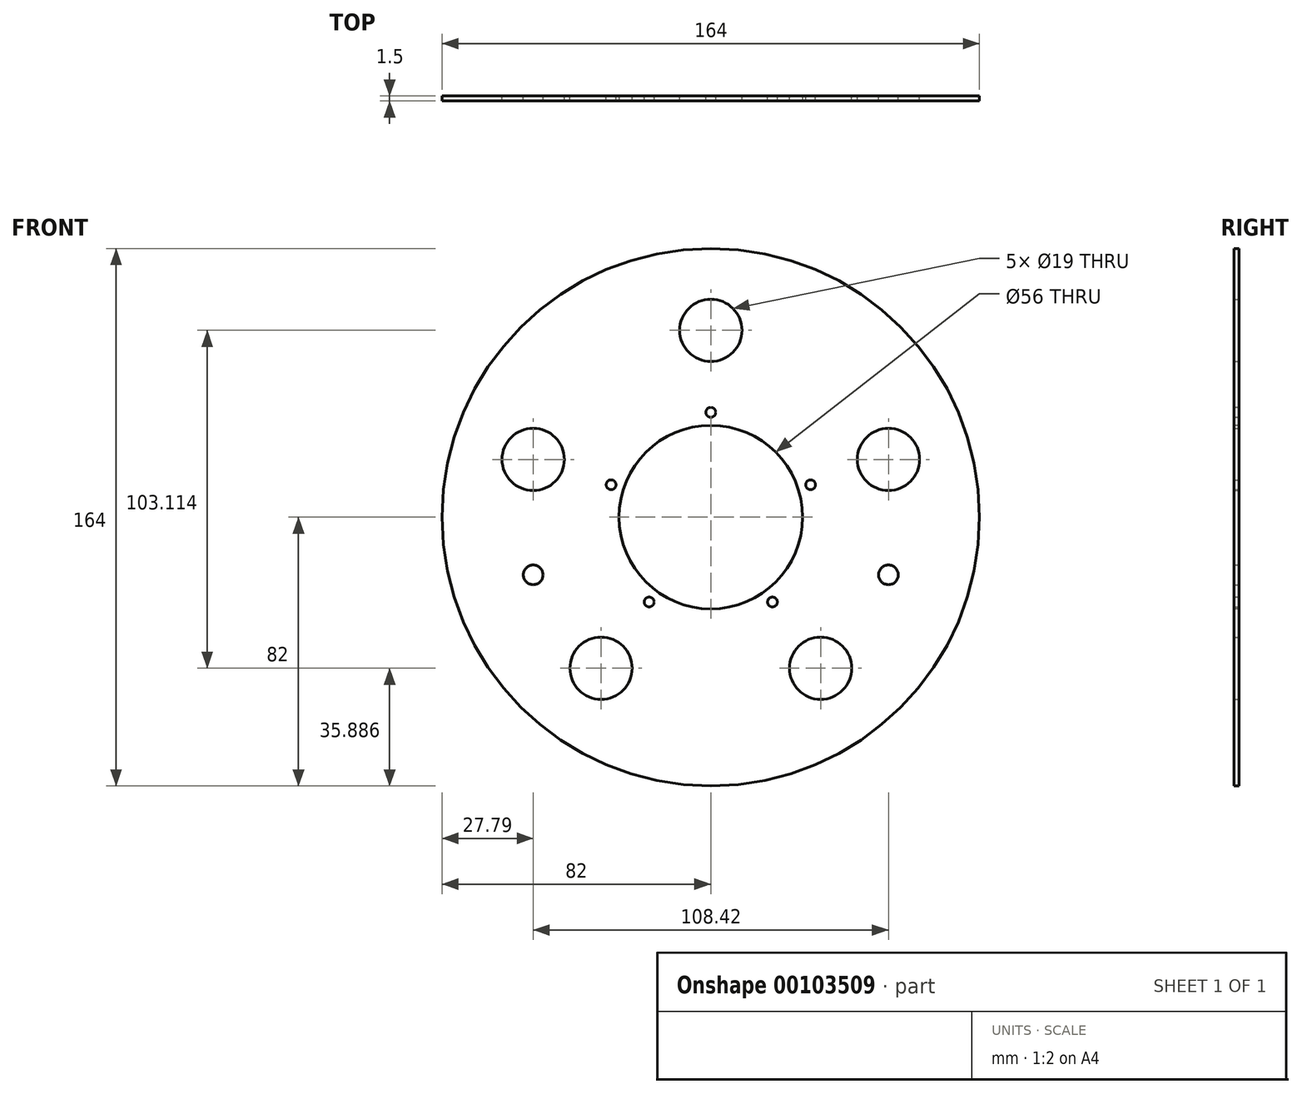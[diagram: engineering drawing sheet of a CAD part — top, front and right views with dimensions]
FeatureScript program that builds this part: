
annotation { "Feature Type Name" : "Feature", "Feature Type Description" : "" }
export const myFeature = defineFeature(function(context is Context, id is Id, definition is map)
    precondition{}
    {
        {
            var Q0;
            Q0=qCreatedBy(makeId("Front.planeOp"),FACE);
            var sketch = newSketch(context, id + "F0", { "sketchPlane" : qUnion([Q0])});
            skCircle(sketch, "E0", {"center": v(0, 0) * mm, "radius": 82 * mm});
            skCircle(sketch, "E1", {"center": v(0, 0) * mm, "radius": 57 * mm, "construction": true});
            skPoint(sketch, "E2", {"position": v(0, 57) * mm});
            skPoint(sketch, "E3", {"position": v(54.21, 17.61) * mm});
            skPoint(sketch, "E4", {"position": v(-54.21, 17.61) * mm});
            skPoint(sketch, "E5", {"position": v(-33.5, -46.11) * mm});
            skPoint(sketch, "E6", {"position": v(33.5, -46.11) * mm});
            skPoint(sketch, "E7", {"position": v(-54.21, -17.61) * mm});
            skPoint(sketch, "E8", {"position": v(54.21, -17.61) * mm});
            skLineSegment(sketch, "E9", {"start": v(0, 0) * mm, "end": v(-54.21, 17.61) * mm, "construction": true});
            skLineSegment(sketch, "E10", {"start": v(0, 0) * mm, "end": v(-54.21, -17.61) * mm, "construction": true});
            skCircle(sketch, "E11", {"center": v(0, 0) * mm, "radius": 32 * mm});
            skLineSegment(sketch, "E12", {"start": v(33.5, -46.11) * mm, "end": v(0, 0) * mm, "construction": true});
            skLineSegment(sketch, "E13", {"start": v(0, 0) * mm, "end": v(-33.5, -46.11) * mm, "construction": true});
            skLineSegment(sketch, "E14", {"start": v(0, 0) * mm, "end": v(0, 57) * mm, "construction": true});
            skLineSegment(sketch, "E15", {"start": v(0, 0) * mm, "end": v(54.21, 17.61) * mm, "construction": true});
            skPoint(sketch, "E16", {"position": v(18.8, -25.89) * mm});
            skPoint(sketch, "E17", {"position": v(30.43, 9.89) * mm});
            skPoint(sketch, "E18", {"position": v(-18.8, -25.89) * mm});
            skPoint(sketch, "E19", {"position": v(-30.43, 9.89) * mm});
            skPoint(sketch, "E20", {"position": v(0, 32) * mm});
            skCircle(sketch, "E21", {"center": v(0, 0) * mm, "radius": 28 * mm});
            skSolve(sketch);
        }
        {
            var Q0;
            Q0=makeQuery(id+"F0.imprint","IMPRINT",FACE,{"disambiguationData":[TD([[makeQuery(id+"F0.imprint","IMPRINT",EDGE,{"derivedFrom":sQuery(id+"F0.wireOp",EDGE,"E11")}),1.0]])]});
            var Q1;
            Q1=makeQuery(id+"F0.imprint","IMPRINT",FACE,{"disambiguationData":[TD([[makeQuery(id+"F0.imprint","IMPRINT",EDGE,{"derivedFrom":sQuery(id+"F0.wireOp",EDGE,"E0")}),1.0]])]});
            extrude(context, id + "F1", {"entities" : qUnion([Q0, Q1]), "oppositeDirection" : true, "depth" : 1.5 * mm});
        }
        {
            var Q0;
            Q0=sQuery(id+"F0.wireOp",VERTEX,"E2");
            var Q1;
            Q1=sQuery(id+"F0.wireOp",VERTEX,"E3");
            var Q2;
            Q2=sQuery(id+"F0.wireOp",VERTEX,"E6");
            var Q3;
            Q3=sQuery(id+"F0.wireOp",VERTEX,"E5");
            var Q4;
            Q4=sQuery(id+"F0.wireOp",VERTEX,"E4");
            var Q5;
            Q5=makeQuery(id+"F1.opExtrude","SWEPT_BODY",BODY,{"disambiguationData":[OSD([sQuery(id+"F0.wireOp",EDGE,"E0")])]});
            hole(context, id + "F2", {"style" : HoleStyle.SIMPLE, "endStyle" : HoleEndStyle.THROUGH, "standardTappedOrClearance" : lookupTablePath({ "standard" : "ISO", "size" : "19", "type" : "Drilled" }), "standardBlindInLast" : lookupTablePath({ "standard" : "ISO", "size" : "19", "type" : "Drilled" }), "holeDiameter" : 19 * mm, "locations" : qUnion([Q0, Q1, Q2, Q3, Q4]), "scope" : qUnion([Q5]), "isTappedThrough" : true, "startStyle" : HoleStartStyle.PART});
        }
        {
            var Q0;
            Q0=sQuery(id+"F0.wireOp",VERTEX,"E7");
            var Q1;
            Q1=sQuery(id+"F0.wireOp",VERTEX,"E8");
            var Q2;
            Q2=makeQuery(id+"F1.opExtrude","SWEPT_BODY",BODY,{"disambiguationData":[OSD([sQuery(id+"F0.wireOp",EDGE,"E0")])]});
            hole(context, id + "F3", {"style" : HoleStyle.SIMPLE, "endStyle" : HoleEndStyle.THROUGH, "standardTappedOrClearance" : lookupTablePath({ "standard" : "ISO", "size" : "6", "type" : "Drilled" }), "standardBlindInLast" : lookupTablePath({ "standard" : "ISO", "size" : "6", "type" : "Drilled" }), "holeDiameter" : 6 * mm, "locations" : qUnion([Q0, Q1]), "scope" : qUnion([Q2]), "isTappedThrough" : true, "startStyle" : HoleStartStyle.SKETCH});
        }
        {
            var Q0;
            Q0=sQuery(id+"F0.wireOp",VERTEX,"E16");
            var Q1;
            Q1=sQuery(id+"F0.wireOp",VERTEX,"E17");
            var Q2;
            Q2=sQuery(id+"F0.wireOp",VERTEX,"E18");
            var Q3;
            Q3=sQuery(id+"F0.wireOp",VERTEX,"E19");
            var Q4;
            Q4=sQuery(id+"F0.wireOp",VERTEX,"E20");
            var Q5;
            Q5=makeQuery(id+"F1.opExtrude","SWEPT_BODY",BODY,{"disambiguationData":[OSD([sQuery(id+"F0.wireOp",EDGE,"E0")])]});
            hole(context, id + "F4", {"style" : HoleStyle.SIMPLE, "endStyle" : HoleEndStyle.THROUGH, "standardTappedOrClearance" : lookupTablePath({ "standard" : "ISO", "size" : "3", "type" : "Drilled" }), "standardBlindInLast" : lookupTablePath({ "standard" : "ISO", "size" : "3", "type" : "Drilled" }), "holeDiameter" : 3 * mm, "locations" : qUnion([Q0, Q1, Q2, Q3, Q4]), "scope" : qUnion([Q5]), "isTappedThrough" : true, "startStyle" : HoleStartStyle.SKETCH});
        }
    });
